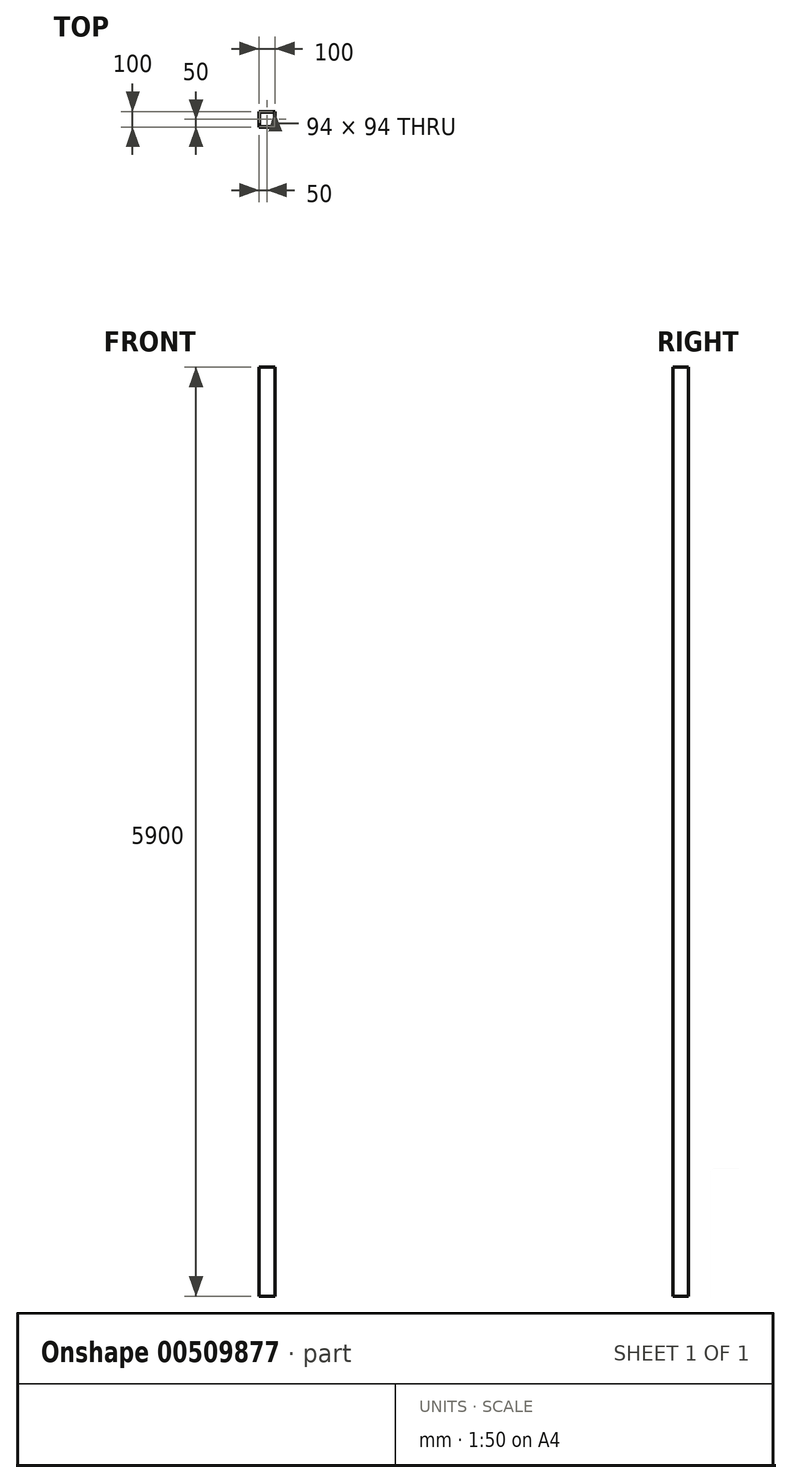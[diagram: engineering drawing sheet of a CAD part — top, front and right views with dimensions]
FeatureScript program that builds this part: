
annotation { "Feature Type Name" : "Feature", "Feature Type Description" : "" }
export const myFeature = defineFeature(function(context is Context, id is Id, definition is map)
    precondition{}
    {
        {
            var Q0;
            Q0=qCreatedBy(makeId("Top.planeOp"),FACE);
            var sketch = newSketch(context, id + "F0", { "sketchPlane" : qUnion([Q0])});
            skLineSegment(sketch, "E0.bottom", {"start": v(50, -50) * mm, "end": v(-50, -50) * mm});
            skLineSegment(sketch, "E0.top", {"start": v(50, 50) * mm, "end": v(-50, 50) * mm});
            skLineSegment(sketch, "E0.left", {"start": v(50, -50) * mm, "end": v(50, 50) * mm});
            skLineSegment(sketch, "E0.right", {"start": v(-50, -50) * mm, "end": v(-50, 50) * mm});
            skPoint(sketch, "E0.middle", {"position": v(0, 0) * mm});
            skLineSegment(sketch, "E1.bottom", {"start": v(47, -47) * mm, "end": v(-47, -47) * mm});
            skLineSegment(sketch, "E1.top", {"start": v(47, 47) * mm, "end": v(-47, 47) * mm});
            skLineSegment(sketch, "E1.left", {"start": v(47, -47) * mm, "end": v(47, 47) * mm});
            skLineSegment(sketch, "E1.right", {"start": v(-47, -47) * mm, "end": v(-47, 47) * mm});
            skSolve(sketch);
        }
        {
            var Q0;
            Q0=makeQuery(id+"F0.imprint","IMPRINT",FACE,{"disambiguationData":[TD([[makeQuery(id+"F0.imprint","IMPRINT",EDGE,{"derivedFrom":sQuery(id+"F0.wireOp",EDGE,"E0.bottom")}),-1.0]])]});
            extrude(context, id + "F1", {"entities" : qUnion([Q0]), "depth" : 5900 * mm, "offsetDistance" : 25 * mm});
        }
    });
